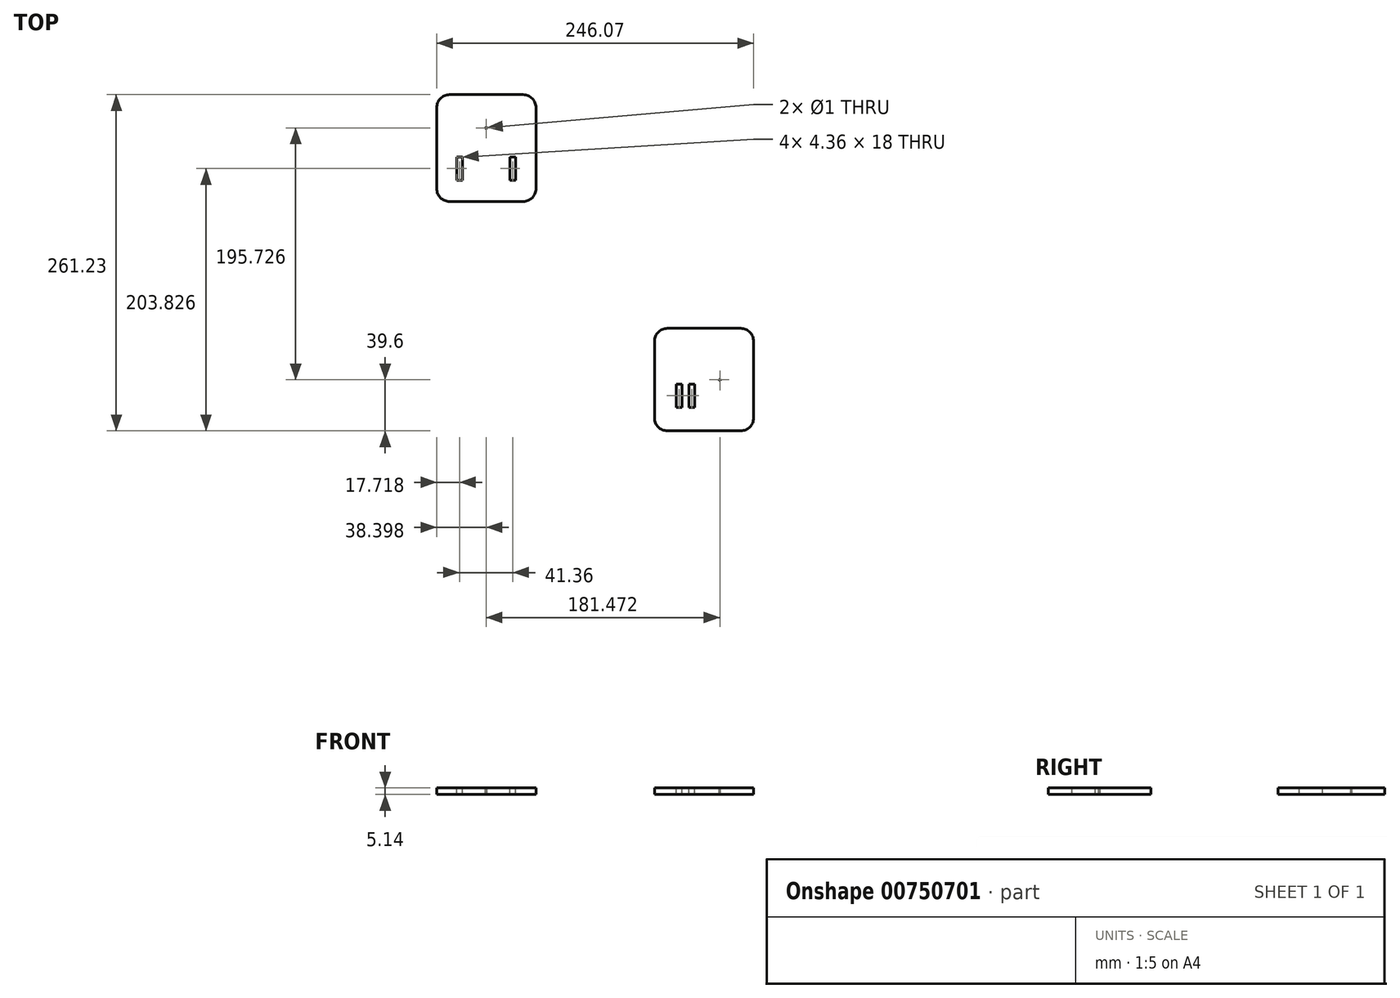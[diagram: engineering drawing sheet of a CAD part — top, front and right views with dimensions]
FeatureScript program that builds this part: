
annotation { "Feature Type Name" : "Feature", "Feature Type Description" : "" }
export const myFeature = defineFeature(function(context is Context, id is Id, definition is map)
    precondition{}
    {
        {
            var Q0;
            Q0=qCreatedBy(makeId("Top.planeOp"),FACE);
            var sketch = newSketch(context, id + "F0", { "sketchPlane" : qUnion([Q0])});
            skLineSegment(sketch, "E0.bottom", {"start": v(10, 0) * mm, "end": v(67, 0) * mm});
            skLineSegment(sketch, "E0.top", {"start": v(10, 79.6) * mm, "end": v(67, 79.6) * mm});
            skLineSegment(sketch, "E0.left", {"start": v(0, 10) * mm, "end": v(0, 69.6) * mm});
            skLineSegment(sketch, "E0.right", {"start": v(77, 10) * mm, "end": v(77, 69.6) * mm});
            skPoint(sketch, "E1.visualSharp", {"position": v(0, 79.6) * mm});
            skArc(sketch, "E1.filletArc", {"start": v(10, 79.6) * mm, "mid": v(2.93, 76.67) * mm, "end": v(0, 69.6) * mm});
            skPoint(sketch, "E2.visualSharp", {"position": v(0, 0) * mm});
            skArc(sketch, "E2.filletArc", {"start": v(0, 10) * mm, "mid": v(2.93, 2.93) * mm, "end": v(10, 0) * mm});
            skPoint(sketch, "E3.visualSharp", {"position": v(77, 0) * mm});
            skArc(sketch, "E3.filletArc", {"start": v(67, 0) * mm, "mid": v(74.07, 2.93) * mm, "end": v(77, 10) * mm});
            skPoint(sketch, "E4.visualSharp", {"position": v(77, 79.6) * mm});
            skArc(sketch, "E4.filletArc", {"start": v(77, 69.6) * mm, "mid": v(74.07, 76.67) * mm, "end": v(67, 79.6) * mm});
            skPoint(sketch, "E5", {"position": v(50.8, 39.6) * mm});
            skLineSegment(sketch, "E6.bottom", {"start": v(-159.07, 178.23) * mm, "end": v(-101.97, 178.23) * mm});
            skLineSegment(sketch, "E6.top", {"start": v(-159.07, 261.23) * mm, "end": v(-101.97, 261.23) * mm});
            skLineSegment(sketch, "E6.left", {"start": v(-169.07, 188.23) * mm, "end": v(-169.07, 251.23) * mm});
            skLineSegment(sketch, "E6.right", {"start": v(-91.97, 188.23) * mm, "end": v(-91.97, 251.23) * mm});
            skPoint(sketch, "E7.visualSharp", {"position": v(-169.07, 261.23) * mm});
            skArc(sketch, "E7.filletArc", {"start": v(-159.07, 261.23) * mm, "mid": v(-166.14, 258.3) * mm, "end": v(-169.07, 251.23) * mm});
            skPoint(sketch, "E8.visualSharp", {"position": v(-169.07, 178.23) * mm});
            skArc(sketch, "E8.filletArc", {"start": v(-169.07, 188.23) * mm, "mid": v(-166.14, 181.16) * mm, "end": v(-159.07, 178.23) * mm});
            skPoint(sketch, "E9.visualSharp", {"position": v(-91.97, 178.23) * mm});
            skArc(sketch, "E9.filletArc", {"start": v(-101.97, 178.23) * mm, "mid": v(-94.9, 181.16) * mm, "end": v(-91.97, 188.23) * mm});
            skPoint(sketch, "E10.visualSharp", {"position": v(-91.97, 261.23) * mm});
            skArc(sketch, "E10.filletArc", {"start": v(-91.97, 251.23) * mm, "mid": v(-94.9, 258.3) * mm, "end": v(-101.97, 261.23) * mm});
            skPoint(sketch, "E11", {"position": v(-130.67, 235.33) * mm});
            skLineSegment(sketch, "E12.bottom", {"start": v(33.3, 57.1) * mm, "end": v(68.3, 57.1) * mm});
            skLineSegment(sketch, "E12.top", {"start": v(33.3, 22.1) * mm, "end": v(68.3, 22.1) * mm});
            skLineSegment(sketch, "E12.left", {"start": v(33.3, 57.1) * mm, "end": v(33.3, 22.1) * mm});
            skLineSegment(sketch, "E12.right", {"start": v(68.3, 57.1) * mm, "end": v(68.3, 22.1) * mm});
            skPoint(sketch, "E13.positionSnap0", {"position": v(50.8, 57.1) * mm});
            skPoint(sketch, "E14", {"position": v(33.3, 39.6) * mm});
            skLineSegment(sketch, "E15.bottom", {"start": v(-148.17, 252.83) * mm, "end": v(-113.17, 252.83) * mm});
            skLineSegment(sketch, "E15.top", {"start": v(-148.17, 217.83) * mm, "end": v(-113.17, 217.83) * mm});
            skLineSegment(sketch, "E15.left", {"start": v(-148.17, 252.83) * mm, "end": v(-148.17, 217.83) * mm});
            skLineSegment(sketch, "E15.right", {"start": v(-113.17, 252.83) * mm, "end": v(-113.17, 217.83) * mm});
            skPoint(sketch, "E16.positionSnap0", {"position": v(-130.67, 252.83) * mm});
            skPoint(sketch, "E17", {"position": v(-148.17, 235.33) * mm});
            skSolve(sketch);
        }
        {
            var Q0;
            Q0=makeQuery(id+"F0.imprint","IMPRINT",FACE,{"disambiguationData":[TD([[makeQuery(id+"F0.imprint","IMPRINT",EDGE,{"derivedFrom":sQuery(id+"F0.wireOp",EDGE,"E6.bottom")}),1.0]])]});
            var Q1;
            Q1=makeQuery(id+"F0.imprint","IMPRINT",FACE,{"disambiguationData":[TD([[makeQuery(id+"F0.imprint","IMPRINT",EDGE,{"derivedFrom":sQuery(id+"F0.wireOp",EDGE,"E0.bottom")}),1.0]])]});
            var Q2;
            Q2=makeQuery(id+"F0.imprint","IMPRINT",FACE,{"disambiguationData":[TD([[makeQuery(id+"F0.imprint","IMPRINT",EDGE,{"derivedFrom":sQuery(id+"F0.wireOp",EDGE,"E12.bottom")}),-1.0]])]});
            var Q3;
            Q3=makeQuery(id+"F0.imprint","IMPRINT",FACE,{"disambiguationData":[TD([[makeQuery(id+"F0.imprint","IMPRINT",EDGE,{"derivedFrom":sQuery(id+"F0.wireOp",EDGE,"E15.bottom")}),-1.0]])]});
            extrude(context, id + "F1", {"entities" : qUnion([Q0, Q1, Q2, Q3]), "depth" : 5.14 * mm, "offsetDistance" : 25 * mm});
        }
        {
            var Q0;
            Q0=makeQuery(id+"F1.opExtrude","CAP_FACE",FACE,{"disambiguationData":[OSD([sQuery(id+"F0.wireOp",EDGE,"E6.bottom"),sQuery(id+"F0.wireOp",EDGE,"E6.top"),sQuery(id+"F0.wireOp",EDGE,"E6.left"),sQuery(id+"F0.wireOp",EDGE,"E6.right"),sQuery(id+"F0.wireOp",EDGE,"E7.filletArc"),sQuery(id+"F0.wireOp",EDGE,"E8.filletArc"),sQuery(id+"F0.wireOp",EDGE,"E9.filletArc"),sQuery(id+"F0.wireOp",EDGE,"E10.filletArc")])],"isStart":false});
            var sketch = newSketch(context, id + "F2", { "sketchPlane" : qUnion([Q0])});
            skLineSegment(sketch, "E18.bottom", {"start": v(-153.53, 212.83) * mm, "end": v(-149.17, 212.83) * mm});
            skLineSegment(sketch, "E18.top", {"start": v(-153.53, 194.83) * mm, "end": v(-149.17, 194.83) * mm});
            skLineSegment(sketch, "E18.left", {"start": v(-153.53, 212.83) * mm, "end": v(-153.53, 194.83) * mm});
            skLineSegment(sketch, "E18.right", {"start": v(-149.17, 212.83) * mm, "end": v(-149.17, 194.83) * mm});
            skLineSegment(sketch, "E19.bottom", {"start": v(-112.17, 212.83) * mm, "end": v(-107.81, 212.83) * mm});
            skLineSegment(sketch, "E19.top", {"start": v(-112.17, 194.83) * mm, "end": v(-107.81, 194.83) * mm});
            skLineSegment(sketch, "E19.left", {"start": v(-112.17, 212.83) * mm, "end": v(-112.17, 194.83) * mm});
            skLineSegment(sketch, "E19.right", {"start": v(-107.81, 212.83) * mm, "end": v(-107.81, 194.83) * mm});
            skLineSegment(sketch, "E20", {"start": v(0, 1.75) * mm, "end": v(0, 16.1) * mm});
            skLineSegment(sketch, "E21", {"start": v(0, 16.1) * mm, "end": v(14.48, 16.1) * mm});
            skLineSegment(sketch, "E22.bottom", {"start": v(17.08, 36.28) * mm, "end": v(21.44, 36.28) * mm});
            skLineSegment(sketch, "E22.top", {"start": v(17.08, 18.28) * mm, "end": v(21.44, 18.28) * mm});
            skLineSegment(sketch, "E22.left", {"start": v(17.08, 36.28) * mm, "end": v(17.08, 18.28) * mm});
            skLineSegment(sketch, "E22.right", {"start": v(21.44, 36.28) * mm, "end": v(21.44, 18.28) * mm});
            skLineSegment(sketch, "E23.bottom", {"start": v(26.94, 36.28) * mm, "end": v(31.3, 36.28) * mm});
            skLineSegment(sketch, "E23.top", {"start": v(26.94, 18.28) * mm, "end": v(31.3, 18.28) * mm});
            skLineSegment(sketch, "E23.left", {"start": v(26.94, 36.28) * mm, "end": v(26.94, 18.28) * mm});
            skLineSegment(sketch, "E23.right", {"start": v(31.3, 36.28) * mm, "end": v(31.3, 18.28) * mm});
            skCircle(sketch, "E24", {"center": v(50.8, 39.6) * mm, "radius": 0.5 * mm});
            skCircle(sketch, "E25", {"center": v(-130.67, 235.33) * mm, "radius": 0.5 * mm});
            skSolve(sketch);
        }
        {
            var Q0;
            Q0 = qSketchRegion(id + "F2", true);
            extrude(context, id + "F3", {"entities" : qUnion([Q0]), "operationType" : NewBodyOperationType.REMOVE, "endBound" : BoundingType.THROUGH_ALL, "oppositeDirection" : true, "depth" : 25 * mm, "offsetDistance" : 25 * mm});
        }
        {
            var Q0;
            Q0=makeQuery(id+"F2.imprint","IMPRINT",FACE,{"disambiguationData":[TD([[makeQuery(id+"F2.imprint","IMPRINT",EDGE,{"derivedFrom":sQuery(id+"F2.wireOp",EDGE,"E22.bottom")}),-1.0]])]});
            var Q1;
            Q1=makeQuery(id+"F2.imprint","IMPRINT",FACE,{"disambiguationData":[TD([[makeQuery(id+"F2.imprint","IMPRINT",EDGE,{"derivedFrom":sQuery(id+"F2.wireOp",EDGE,"E23.bottom")}),-1.0]])]});
            var Q2;
            Q2=makeQuery(id+"F2.imprint","IMPRINT",FACE,{"disambiguationData":[TD([[makeQuery(id+"F2.imprint","IMPRINT",EDGE,{"derivedFrom":sQuery(id+"F2.wireOp",EDGE,"E24")}),1.0]])]});
            extrude(context, id + "F4", {"entities" : qUnion([Q0, Q1, Q2]), "operationType" : NewBodyOperationType.REMOVE, "endBound" : BoundingType.THROUGH_ALL, "oppositeDirection" : true, "depth" : 25 * mm, "offsetDistance" : 25 * mm});
        }
    });
